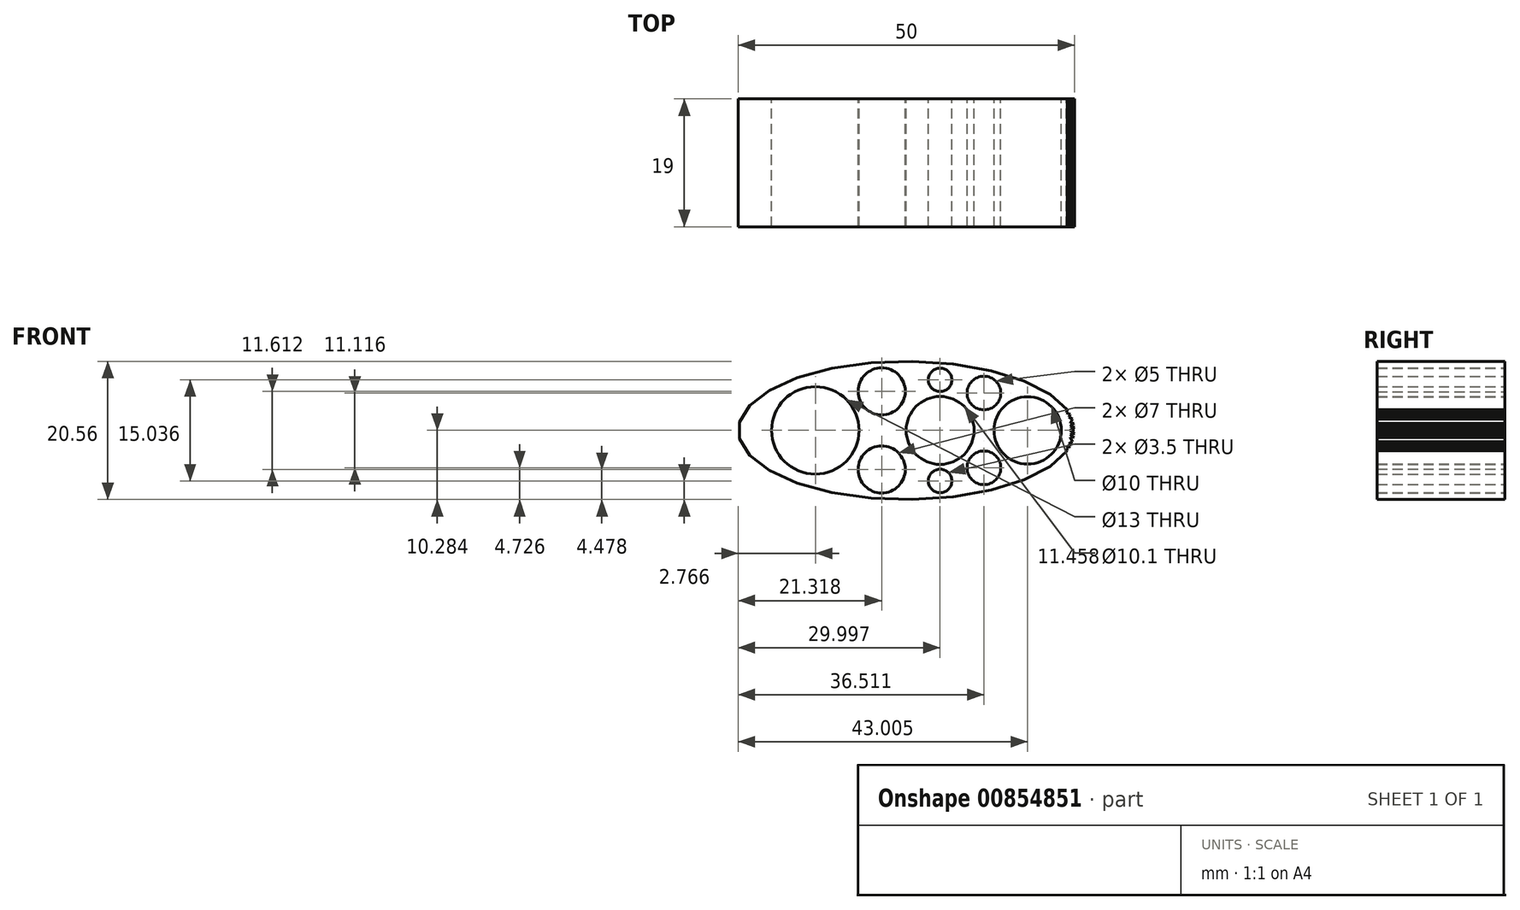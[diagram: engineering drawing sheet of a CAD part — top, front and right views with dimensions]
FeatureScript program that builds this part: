
annotation { "Feature Type Name" : "Feature", "Feature Type Description" : "" }
export const myFeature = defineFeature(function(context is Context, id is Id, definition is map)
    precondition{}
    {
        {
            var Q0;
            Q0=qCreatedBy(makeId("Front.planeOp"),FACE);
            var sketch = newSketch(context, id + "F0", { "sketchPlane" : qUnion([Q0])});
            skLineSegment(sketch, "E0", {"start": v(-59.43, 18.54) * mm, "end": v(-8.43, 18.54) * mm, "construction": true});
            skLineSegment(sketch, "E1", {"start": v(-28.43, 18.54) * mm, "end": v(-28.43, 44) * mm, "construction": true});
            skLineSegment(sketch, "E2", {"start": v(-33.43, 18.54) * mm, "end": v(-33.43, 39.54) * mm, "construction": true});
            skCircle(sketch, "E3", {"center": v(-28.43, 18.54) * mm, "radius": 5.05 * mm});
            skCircle(sketch, "E4", {"center": v(-46.97, 18.54) * mm, "radius": 6.5 * mm});
            skCircle(sketch, "E5", {"center": v(-15.43, 18.54) * mm, "radius": 5 * mm});
            skEllipse(sketch, "E6", {"center": v(-33.43, 18.54) * mm, "majorRadius": 25 * mm, "minorRadius": 10.28 * mm, "majorAxis": v(1, 0)});
            skLineSegment(sketch, "E7", {"start": v(-9.56, 21.6) * mm, "end": v(-9.65, 21.2) * mm});
            skLineSegment(sketch, "E8", {"start": v(-9.65, 21.2) * mm, "end": v(-9.12, 20.94) * mm});
            skLineSegment(sketch, "E9", {"start": v(-9.12, 20.94) * mm, "end": v(-9.28, 20.54) * mm});
            skLineSegment(sketch, "E10", {"start": v(-9.28, 20.54) * mm, "end": v(-8.76, 20.2) * mm});
            skLineSegment(sketch, "E11", {"start": v(-8.76, 20.2) * mm, "end": v(-9.12, 19.56) * mm});
            skLineSegment(sketch, "E12", {"start": v(-9.12, 19.56) * mm, "end": v(-8.56, 19.56) * mm});
            skLineSegment(sketch, "E13", {"start": v(-8.56, 19.56) * mm, "end": v(-9.08, 19.13) * mm});
            skLineSegment(sketch, "E14", {"start": v(-9.08, 19.13) * mm, "end": v(-8.46, 19.03) * mm});
            skLineSegment(sketch, "E15", {"start": v(-8.46, 19.03) * mm, "end": v(-9.08, 18.6) * mm});
            skLineSegment(sketch, "E16", {"start": v(-9.08, 18.6) * mm, "end": v(-8.43, 18.54) * mm});
            skLineSegment(sketch, "E17.MirrorCS", {"start": v(-9.56, 15.5) * mm, "end": v(-9.65, 15.88) * mm});
            skLineSegment(sketch, "E18.MirrorCS", {"start": v(-9.65, 15.88) * mm, "end": v(-9.12, 16.15) * mm});
            skLineSegment(sketch, "E19.MirrorCS", {"start": v(-9.12, 16.15) * mm, "end": v(-9.28, 16.55) * mm});
            skLineSegment(sketch, "E20.MirrorCS", {"start": v(-9.28, 16.55) * mm, "end": v(-8.76, 16.89) * mm});
            skLineSegment(sketch, "E21.MirrorCS", {"start": v(-8.76, 16.89) * mm, "end": v(-9.12, 17.53) * mm});
            skLineSegment(sketch, "E22.MirrorCS", {"start": v(-9.12, 17.53) * mm, "end": v(-8.56, 17.53) * mm});
            skLineSegment(sketch, "E23.MirrorCS", {"start": v(-8.56, 17.53) * mm, "end": v(-9.08, 17.96) * mm});
            skLineSegment(sketch, "E24.MirrorCS", {"start": v(-9.08, 17.96) * mm, "end": v(-8.46, 18.05) * mm});
            skLineSegment(sketch, "E25.MirrorCS", {"start": v(-8.46, 18.05) * mm, "end": v(-9.08, 18.5) * mm});
            skLineSegment(sketch, "E26.MirrorCS", {"start": v(-9.08, 18.5) * mm, "end": v(-8.43, 18.54) * mm});
            skCircle(sketch, "E27", {"center": v(-37.11, 24.35) * mm, "radius": 3.5 * mm});
            skCircle(sketch, "E28", {"center": v(-21.92, 24.1) * mm, "radius": 2.5 * mm});
            skCircle(sketch, "E29.MirrorC", {"center": v(-37.11, 12.74) * mm, "radius": 3.5 * mm});
            skCircle(sketch, "E30.MirrorC", {"center": v(-21.92, 12.99) * mm, "radius": 2.5 * mm});
            skCircle(sketch, "E31", {"center": v(-28.43, 26.06) * mm, "radius": 1.75 * mm});
            skCircle(sketch, "E32.MirrorC", {"center": v(-28.43, 11.03) * mm, "radius": 1.75 * mm});
            skSolve(sketch);
        }
        {
            var Q0;
            Q0=makeQuery(id+"F0.imprint","IMPRINT",FACE,{"disambiguationData":[TD([[makeQuery(id+"F0.imprint","IMPRINT",EDGE,{"derivedFrom":sQuery(id+"F0.wireOp",EDGE,"E3")}),-1.0]])]});
            extrude(context, id + "F1", {"entities" : qUnion([Q0]), "depth" : 19 * mm, "offsetDistance" : 25 * mm});
        }
    });
